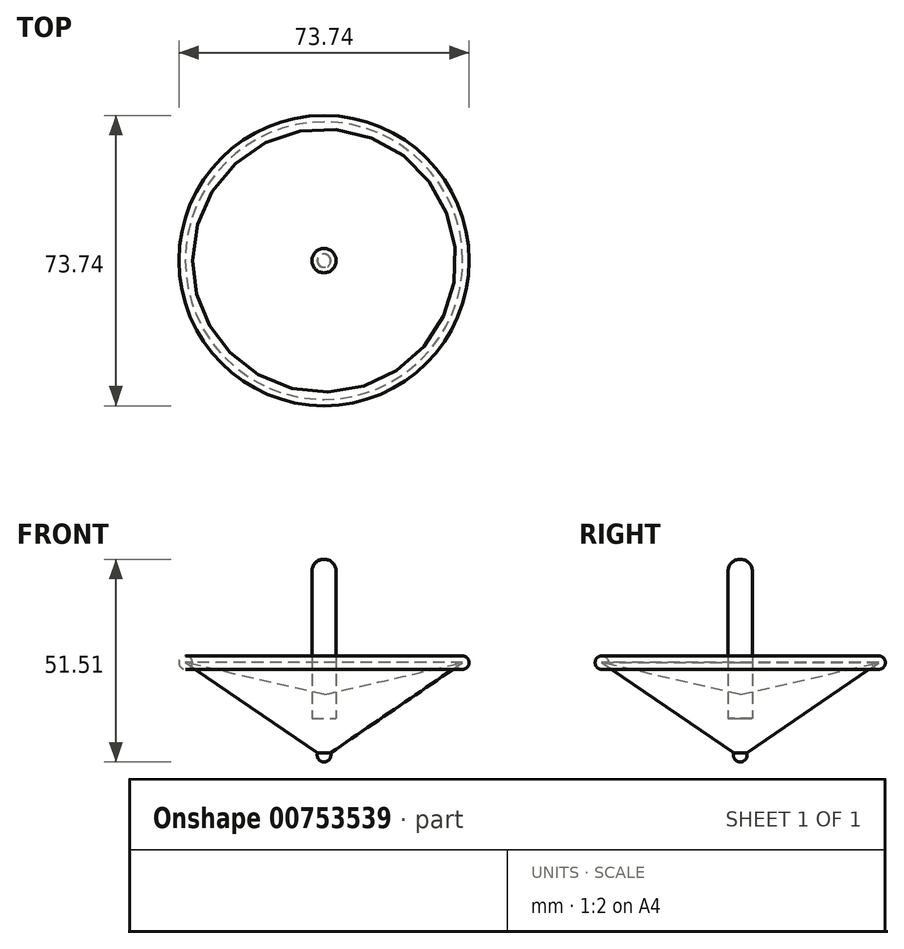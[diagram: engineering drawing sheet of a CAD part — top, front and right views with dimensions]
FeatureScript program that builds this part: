
annotation { "Feature Type Name" : "Feature", "Feature Type Description" : "" }
export const myFeature = defineFeature(function(context is Context, id is Id, definition is map)
    precondition{}
    {
        {
            var Q0;
            Q0=qCreatedBy(makeId("Front.planeOp"),FACE);
            var sketch = newSketch(context, id + "F0", { "sketchPlane" : qUnion([Q0])});
            skLineSegment(sketch, "E0", {"start": v(0, -24.07) * mm, "end": v(-35.24, 0) * mm});
            skLineSegment(sketch, "E1", {"start": v(-35.24, 0) * mm, "end": v(0, -8.13) * mm});
            skLineSegment(sketch, "E2", {"start": v(0, -8.13) * mm, "end": v(0, -24.07) * mm});
            skSolve(sketch);
        }
        {
            var Q0;
            Q0 = qSketchRegion(id + "F0", true);
            var Q1;
            Q1=sQuery(id+"F0.wireOp",EDGE,"E2");
            revolve(context, id + "F1", {"surfaceOperationType" : NewSurfaceOperationType.NEW, "entities" : qUnion([Q0]), "axis" : qUnion([Q1]), "revolveType" : RevolveType.FULL});
        }
        {
            var Q0;
            Q0=qCreatedBy(makeId("Front.planeOp"),FACE);
            var sketch = newSketch(context, id + "F2", { "sketchPlane" : qUnion([Q0])});
            skLineSegment(sketch, "E3.bottom", {"start": v(0, -14.23) * mm, "end": v(-3.09, -14.23) * mm});
            skLineSegment(sketch, "E3.top", {"start": v(0, 23.18) * mm, "end": v(-3.09, 23.18) * mm});
            skLineSegment(sketch, "E3.left", {"start": v(0, -14.23) * mm, "end": v(0, 23.18) * mm});
            skLineSegment(sketch, "E3.right", {"start": v(-3.09, -14.23) * mm, "end": v(-3.09, 23.18) * mm});
            skCircle(sketch, "E4", {"center": v(0, 23.18) * mm, "radius": 3.09 * mm});
            skLineSegment(sketch, "E5", {"start": v(0, 23.18) * mm, "end": v(0, 26.27) * mm});
            skSolve(sketch);
        }
        {
            var Q0;
            {var subQ0=sQuery(id+"F2.wireOp",EDGE,"E3.bottom");Q0=makeQuery(id+"F2.imprint","IMPRINT",FACE,{"disambiguationData":[TD([[makeQuery(id+"F2.imprint","IMPRINT",EDGE,{"derivedFrom":subQ0}),-1.0]])]});}
            var Q1;
            {var subQ0=sQuery(id+"F2.wireOp",EDGE,"E3.top");Q1=makeQuery(id+"F2.imprint","IMPRINT",FACE,{"disambiguationData":[TD([[makeQuery(id+"F2.imprint","IMPRINT",EDGE,{"derivedFrom":subQ0}),1.0]])]});}
            var Q2;
            {var subQ0=sQuery(id+"F2.wireOp",EDGE,"E3.top");Q2=makeQuery(id+"F2.imprint","IMPRINT",FACE,{"disambiguationData":[TD([[makeQuery(id+"F2.imprint","IMPRINT",EDGE,{"derivedFrom":subQ0}),-1.0]])]});}
            var Q3;
            Q3=sQuery(id+"F2.wireOp",EDGE,"E3.left");
            revolve(context, id + "F3", {"surfaceOperationType" : NewSurfaceOperationType.NEW, "entities" : qUnion([Q0, Q1, Q2]), "axis" : qUnion([Q3]), "revolveType" : RevolveType.FULL});
        }
        {
            var Q0;
            Q0=qCreatedBy(makeId("Front.planeOp"),FACE);
            var sketch = newSketch(context, id + "F4", { "sketchPlane" : qUnion([Q0])});
            skCircle(sketch, "E6", {"center": v(0, -23.5) * mm, "radius": 1.74 * mm});
            skLineSegment(sketch, "E7", {"start": v(0, -25.24) * mm, "end": v(0, -21.76) * mm});
            skSolve(sketch);
        }
        {
            var Q0;
            {var subQ0=sQuery(id+"F4.wireOp",EDGE,"E7");Q0=makeQuery(id+"F4.imprint","IMPRINT",FACE,{"disambiguationData":[TD([[makeQuery(id+"F4.imprint","IMPRINT",EDGE,{"derivedFrom":subQ0}),1.0]])]});}
            var Q1;
            Q1=sQuery(id+"F4.wireOp",EDGE,"E7");
            revolve(context, id + "F5", {"operationType" : NewBodyOperationType.ADD, "surfaceOperationType" : NewSurfaceOperationType.NEW, "entities" : qUnion([Q0]), "axis" : qUnion([Q1]), "revolveType" : RevolveType.FULL});
        }
        {
            var Q0;
            Q0=qCreatedBy(makeId("Front.planeOp"),FACE);
            var sketch = newSketch(context, id + "F6", { "sketchPlane" : qUnion([Q0])});
            skCircle(sketch, "E8", {"center": v(-35.16, 0) * mm, "radius": 1.71 * mm});
            skLineSegment(sketch, "E9", {"start": v(0, 0) * mm, "end": v(0, 4.42) * mm});
            skSolve(sketch);
        }
        {
            var Q0;
            Q0=makeQuery(id+"F6.imprint","IMPRINT",FACE,{"disambiguationData":[TD([[makeQuery(id+"F6.imprint","IMPRINT",EDGE,{"derivedFrom":sQuery(id+"F6.wireOp",EDGE,"E8")}),1.0]])]});
            var Q1;
            Q1=sQuery(id+"F6.wireOp",EDGE,"E9");
            revolve(context, id + "F7", {"surfaceOperationType" : NewSurfaceOperationType.NEW, "entities" : qUnion([Q0]), "axis" : qUnion([Q1]), "revolveType" : RevolveType.FULL});
        }
    });
